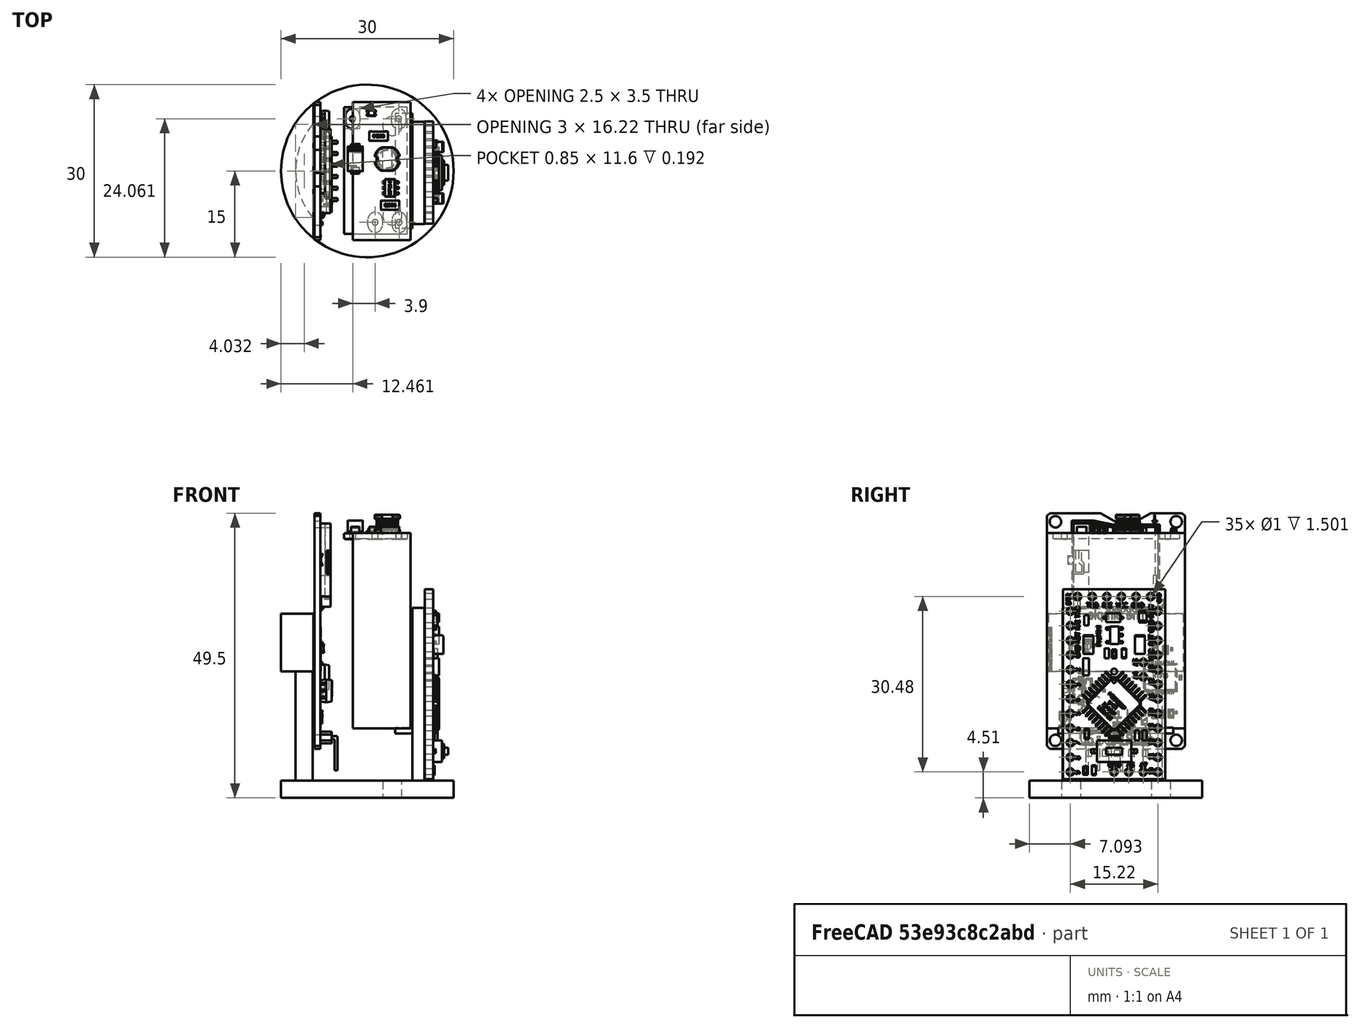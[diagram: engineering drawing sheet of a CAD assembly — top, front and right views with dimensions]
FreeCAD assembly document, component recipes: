
FREECAD ASSEMBLY — COMPONENT RECIPES ("case")

This assembly document has 2 components, labeled P0..P1 below (a component is one placed body or linked part). 2 of them carry a construction recipe — the FreeCAD feature program that regenerates the part from scratch, quoted from this document or its linked companion documents; the rest are supplied as boundary geometry only. No exploded tour is included for this assembly.
COMPONENT P0 — recipe-attached ("Case", modeled in this document).
Construction recipe (the document's own serialized feature program — sketch geometry with constraints, then the solid features built on it; lengths are millimeters unless a unit is written):

FEATURE [Sketcher::SketchObject] Sketch001
  ArcFitTolerance = 1e-06
  AttachmentSupport = -> [XY_Plane001]
  FullyConstrained = true
  MakeInternals = false
  MapMode = 5
  sketch-geometry (1):
    g0: Circle CenterX=0 CenterY=0 CenterZ=0 NormalX=0 NormalY=0 NormalZ=1 AngleXU=0 Radius=16.5
  constraints (2):
    c: Diameter(g0) = 33
    c: Coincident(g0,g-1)
FEATURE [PartDesign::Pad] Pad
  Direction = (0,0,1)
  Length = 1
  Length2 = 10
  Profile = -> Sketch001
  ReferenceAxis = -> Sketch001 [N_Axis]
  Refine = true
  Suppressed = false
  Type = 0
FEATURE [Sketcher::SketchObject] Sketch003
  ArcFitTolerance = 1e-06
  AttachmentSupport = -> [XY_Plane001]
  FullyConstrained = false
  MakeInternals = false
  MapMode = 5
  sketch-geometry (4):
    g0: LineSegment StartX=-10.1025 StartY=7.19243 StartZ=0 EndX=-10.8313 EndY=7.19243 EndZ=0
    g1: LineSegment StartX=-10.8313 StartY=7.19243 StartZ=0 EndX=-10.8313 EndY=-7.43647 EndZ=0
    g2: LineSegment StartX=-10.8313 StartY=-7.43647 StartZ=0 EndX=-10.1025 EndY=-7.43647 EndZ=0
    g3: LineSegment StartX=-10.1025 StartY=-7.43647 StartZ=0 EndX=-10.1025 EndY=7.19243 EndZ=0
  constraints (8):
    c: Coincident(g0,g1)
    c: Coincident(g1,g2)
    c: Coincident(g2,g3)
    c: Coincident(g3,g0)
    c: Horizontal(g0)
    c: Horizontal(g2)
    c: Vertical(g1)
    c: Vertical(g3)
FEATURE [Sketcher::SketchObject] Sketch004
  ArcFitTolerance = 1e-06
  AttachmentSupport = -> [Pad]
  FullyConstrained = false
  MakeInternals = false
  MapMode = 5
  Placement = pos=(0,0,1) rot=(0,0,1;0rad)
  sketch-geometry (4):
    g0: LineSegment StartX=-10.0742 StartY=4.3685 StartZ=0 EndX=-11.0742 EndY=4.3685 EndZ=0
    g1: LineSegment StartX=-11.0742 StartY=4.3685 StartZ=0 EndX=-11.0742 EndY=-5.47094 EndZ=0
    g2: LineSegment StartX=-11.0742 StartY=-5.47094 StartZ=0 EndX=-10.0742 EndY=-5.47094 EndZ=0
    g3: LineSegment StartX=-10.0742 StartY=-5.47094 StartZ=0 EndX=-10.0742 EndY=4.3685 EndZ=0
  constraints (9):
    c: Coincident(g0,g1)
    c: Coincident(g1,g2)
    c: Coincident(g2,g3)
    c: Coincident(g3,g0)
    c: Horizontal(g0)
    c: Horizontal(g2)
    c: Vertical(g1)
    c: Vertical(g3)
    c: Distance(g1,g3) = 1
FEATURE [PartDesign::Pocket] Pocket
  BaseFeature = -> Pad
  Direction = (0,0,-1)
  Length = 5
  Length2 = 5
  Profile = -> Sketch004
  ReferenceAxis = -> Sketch004 [N_Axis]
  Refine = true
  Suppressed = false
  Type = 0
FEATURE [Sketcher::SketchObject] Sketch005
  ArcFitTolerance = 1e-06
  AttachmentSupport = -> [Pocket]
  FullyConstrained = false
  MakeInternals = false
  MapMode = 5
  Placement = pos=(0,0,1) rot=(0,0,1;0rad)
  sketch-geometry (4):
    g0: LineSegment StartX=9.95573 StartY=8.56673 StartZ=0 EndX=7.83459 EndY=8.56673 EndZ=0
    g1: LineSegment StartX=7.83459 StartY=8.56673 StartZ=0 EndX=7.83459 EndY=-9.23192 EndZ=0
    g2: LineSegment StartX=7.83459 StartY=-9.23192 StartZ=0 EndX=9.95573 EndY=-9.23192 EndZ=0
    g3: LineSegment StartX=9.95573 StartY=-9.23192 StartZ=0 EndX=9.95573 EndY=8.56673 EndZ=0
  constraints (8):
    c: Coincident(g0,g1)
    c: Coincident(g1,g2)
    c: Coincident(g2,g3)
    c: Coincident(g3,g0)
    c: Horizontal(g0)
    c: Horizontal(g2)
    c: Vertical(g1)
    c: Vertical(g3)
FEATURE [PartDesign::Pad] Pad002
  BaseFeature = -> Pocket
  Direction = (0,0,1)
  Length = 30
  Length2 = 10
  Profile = -> Sketch005
  ReferenceAxis = -> Sketch005 [N_Axis]
  Refine = true
  Suppressed = false
  Type = 0
FEATURE [Sketcher::SketchObject] Sketch006
  ArcFitTolerance = 1e-06
  AttachmentSupport = -> [Pad002]
  FullyConstrained = false
  MakeInternals = false
  MapMode = 5
  Placement = pos=(0,0,0) rot=(1,0,0;3.14159rad)
  sketch-geometry (2):
    g0: LineSegment StartX=-9.46997 StartY=8.10814 StartZ=0 EndX=-9.46997 EndY=-8.10814 EndZ=0
    g1: ArcOfCircle CenterX=0 CenterY=0 CenterZ=0 NormalX=0 NormalY=0 NormalZ=1 AngleXU=0 Radius=12.4668 StartAngle=2.43351 EndAngle=3.84967
  constraints (3):
    c: Vertical(g0)
    c: Coincident(g1,g0)
    c: Coincident(g1,g0)
FEATURE [PartDesign::Pad] Pad003
  BaseFeature = -> Pad002
  Direction = (0,0,-1)
  Length = 30
  Length2 = 10
  Profile = -> Sketch006
  ReferenceAxis = -> Sketch006 [N_Axis]
  Refine = true
  Reversed = true
  Suppressed = false
  Type = 0
FEATURE [Sketcher::SketchObject] Sketch007
  ArcFitTolerance = 1e-06
  AttachmentSupport = -> [Pad003]
  FullyConstrained = false
  MakeInternals = false
  MapMode = 5
  Placement = pos=(7.83459,0,0) rot=(0.57735,-0.57735,-0.57735;2.0944rad)
  sketch-geometry (4):
    g0: LineSegment StartX=-10 StartY=6.21939 StartZ=0 EndX=-10 EndY=5.1638 EndZ=0
    g1: LineSegment StartX=-10 StartY=5.1638 StartZ=0 EndX=10 EndY=5.1638 EndZ=0
    g2: LineSegment StartX=10 StartY=5.1638 StartZ=0 EndX=10 EndY=6.21939 EndZ=0
    g3: LineSegment StartX=10 StartY=6.21939 StartZ=0 EndX=-10 EndY=6.21939 EndZ=0
  constraints (8):
    c: Coincident(g0,g1)
    c: Coincident(g1,g2)
    c: Coincident(g2,g3)
    c: Coincident(g3,g0)
    c: Vertical(g0)
    c: Vertical(g2)
    c: Horizontal(g1)
    c: Horizontal(g3)
FEATURE [PartDesign::Pad] Pad004
  BaseFeature = -> Pad003
  Direction = (-1,0,0)
  Length = 3
  Length2 = 10
  Profile = -> Sketch007
  ReferenceAxis = -> Sketch007 [N_Axis]
  Refine = true
  Suppressed = false
  Type = 0
FEATURE [Sketcher::SketchObject] Sketch
  ArcFitTolerance = 1e-06
  AttachmentSupport = -> [Pad004]
  FullyConstrained = false
  MakeInternals = false
  MapMode = 5
  Placement = pos=(0,0,30) rot=(0,0,1;0rad)
  sketch-geometry (2):
    g0: ArcOfCircle CenterX=0 CenterY=-0.00563305 CenterZ=0 NormalX=0 NormalY=0 NormalZ=1 AngleXU=0 Radius=16.4954 StartAngle=2.17527 EndAngle=4.10791
    g1: LineSegment StartX=-9.37485 StartY=13.5667 StartZ=0 EndX=-9.37485 EndY=-13.578 EndZ=0
  constraints (3):
    c: Coincident(g1,g0)
    c: Coincident(g1,g0)
    c: Vertical(g1)
FEATURE [PartDesign::Pad] Pad005
  BaseFeature = -> Pad004
  Direction = (0,0,1)
  Length = 10
  Length2 = 10
  Profile = -> Sketch
  ReferenceAxis = -> Sketch [N_Axis]
  Refine = true
  Reversed = true
  Suppressed = false
  Type = 0
FEATURE [Sketcher::SketchObject] Sketch008
  ArcFitTolerance = 1e-06
  AttachmentSupport = -> [Pad005]
  FullyConstrained = false
  MakeInternals = false
  MapMode = 5
  Placement = pos=(0,0,1) rot=(0,0,1;0rad)
  sketch-geometry (2):
    g0: Circle CenterX=4.36794 CenterY=-7.78214 CenterZ=0 NormalX=0 NormalY=0 NormalZ=1 AngleXU=0 Radius=1.55798
    g1: Circle CenterX=4.35381 CenterY=7.76956 CenterZ=0 NormalX=0 NormalY=0 NormalZ=1 AngleXU=0 Radius=1.55627
FEATURE [PartDesign::Pocket] Pocket001
  BaseFeature = -> Pad005
  Direction = (0,0,-1)
  Length = 5
  Length2 = 5
  Profile = -> Sketch008
  ReferenceAxis = -> Sketch008 [N_Axis]
  Refine = true
  Suppressed = false
  Type = 0
FEATURE [PartDesign::Pad] Pad006
  BaseFeature = -> Pocket001
  Direction = (0,0,-1)
  Length = 2
  Length2 = 10
  Profile = -> Pocket001 [Face2]
  Refine = true
  Suppressed = false
  Type = 0
FEATURE [Sketcher::SketchObject] Sketch009
  ArcFitTolerance = 1e-06
  AttachmentSupport = -> [Pad006]
  FullyConstrained = true
  MakeInternals = false
  MapMode = 5
  Placement = pos=(0,0,-2) rot=(1,0,0;3.14159rad)
  sketch-geometry (2):
    g0: Circle CenterX=0 CenterY=0 CenterZ=0 NormalX=0 NormalY=0 NormalZ=1 AngleXU=0 Radius=15.5
    g1: Circle CenterX=0 CenterY=0 CenterZ=0 NormalX=0 NormalY=0 NormalZ=1 AngleXU=0 Radius=16.5
  constraints (4):
    c: Diameter(g0) = 31
    c: Coincident(g0,g-1)
    c: Diameter(g1) = 33
    c: Coincident(g1,g0)
FEATURE [PartDesign::Pocket] Pocket002
  BaseFeature = -> Pad006
  Direction = (0,0,1)
  Length = 300
  Length2 = 5
  Profile = -> Sketch009
  ReferenceAxis = -> Sketch009 [N_Axis]
  Refine = true
  Suppressed = false
  Type = 0
FEATURE [PartDesign::Pad] Pad007
  BaseFeature = -> Pocket002
  Direction = (0,0,1)
  Length = 4
  Length2 = 10
  Profile = -> Pocket002 [Face21]
  Refine = true
  Suppressed = false
  Type = 0
FEATURE [PartDesign::Pocket] Pocket003
  BaseFeature = -> Pad007
  Direction = (0,0,1)
  Length = 4
  Length2 = 5
  Profile = -> Pad007 [Face15]
  Refine = true
  Suppressed = false
  Type = 0
FEATURE [Sketcher::SketchObject] Sketch010
  ArcFitTolerance = 1e-06
  AttachmentSupport = -> [Pocket003]
  FullyConstrained = true
  MakeInternals = false
  MapMode = 5
  Placement = pos=(0,0,-2) rot=(1,0,0;3.14159rad)
  sketch-geometry (2):
    g0: Circle CenterX=0 CenterY=0 CenterZ=0 NormalX=0 NormalY=0 NormalZ=1 AngleXU=0 Radius=15.5
    g1: Circle CenterX=0 CenterY=0 CenterZ=0 NormalX=0 NormalY=0 NormalZ=1 AngleXU=0 Radius=15
  constraints (4):
    c: Diameter(g0) = 31
    c: Coincident(g0,g-1)
    c: Diameter(g1) = 30
    c: Coincident(g1,g0)
FEATURE [PartDesign::Pocket] Pocket004
  BaseFeature = -> Pocket003
  Direction = (0,0,1)
  Length = 600
  Length2 = 5
  Profile = -> Sketch010
  ReferenceAxis = -> Sketch010 [N_Axis]
  Refine = true
  Suppressed = false
  Type = 0
FEATURE [Sketcher::SketchObject] Sketch011
  ArcFitTolerance = 1e-06
  AttachmentSupport = -> [Pocket004]
  FullyConstrained = false
  MakeInternals = false
  MapMode = 5
  Placement = pos=(0,0,-2) rot=(1,0,0;3.14159rad)
  sketch-geometry (4):
    g0: Circle CenterX=4.33918 CenterY=-7.8017 CenterZ=0 NormalX=0 NormalY=0 NormalZ=1 AngleXU=0 Radius=1.58527
    g1: Circle CenterX=4.33918 CenterY=-7.8017 CenterZ=0 NormalX=0 NormalY=0 NormalZ=1 AngleXU=0 Radius=1.65
    g2: Circle CenterX=4.36352 CenterY=7.76627 CenterZ=0 NormalX=0 NormalY=0 NormalZ=1 AngleXU=0 Radius=1.56339
    g3: Circle CenterX=4.36352 CenterY=7.76627 CenterZ=0 NormalX=0 NormalY=0 NormalZ=1 AngleXU=0 Radius=1.65
  constraints (4):
    c: Diameter(g1) = 3.3
    c: Coincident(g1,g0)
    c: Diameter(g3) = 3.3
    c: Coincident(g3,g2)
FEATURE [PartDesign::Pocket] Pocket005
  BaseFeature = -> Pocket004
  Direction = (0,0,1)
  Length = 8
  Length2 = 5
  Profile = -> Sketch011
  ReferenceAxis = -> Sketch011 [N_Axis]
  Refine = true
  Suppressed = false
  Type = 0
FEATURE [PartDesign::Body] Body  label="Case"
  AllowCompound = false
  Group = -> [Sketch001,Pad,Sketch003,Sketch004,Pocket,Sketch005,Pad002,Sketch006,Pad003,Sketch007,Pad004,Sketch,Pad005,Sketch008,Pocket001,Pad006,Sketch009,Pocket002,Pad007,Pocket003,Sketch010,Pocket004,Sketch011,Pocket005]
  Origin = -> Origin001
  Tip = -> Pocket005
COMPONENT P1 — recipe-attached ("lipo", modeled in this document).
Construction recipe (the document's own serialized feature program — sketch geometry with constraints, then the solid features built on it; lengths are millimeters unless a unit is written):

FEATURE [Sketcher::SketchObject] Sketch002
  ArcFitTolerance = 1e-06
  AttachmentSupport = -> [XY_Plane002]
  FullyConstrained = true
  MakeInternals = false
  MapMode = 5
  sketch-geometry (4):
    g0: LineSegment StartX=0 StartY=0 StartZ=0 EndX=0 EndY=-24 EndZ=0
    g1: LineSegment StartX=0 StartY=-24 StartZ=0 EndX=34 EndY=-24 EndZ=0
    g2: LineSegment StartX=34 StartY=-24 StartZ=0 EndX=34 EndY=0 EndZ=0
    g3: LineSegment StartX=34 StartY=0 StartZ=0 EndX=0 EndY=0 EndZ=0
  constraints (11):
    c: Coincident(g0,g1)
    c: Coincident(g1,g2)
    c: Coincident(g2,g3)
    c: Coincident(g3,g0)
    c: Vertical(g0)
    c: Vertical(g2)
    c: Horizontal(g1)
    c: Horizontal(g3)
    c: Distance(g0,g2) = 34
    c: Distance(g1,g3) = 24
    c: Coincident(g0,g-1)
FEATURE [PartDesign::Pad] Pad001
  Direction = (0,0,1)
  Length = 10
  Length2 = 10
  Profile = -> Sketch002
  ReferenceAxis = -> Sketch002 [N_Axis]
  Refine = true
  Suppressed = false
  Type = 0
FEATURE [PartDesign::Body] Body001  label="lipo"
  AllowCompound = false
  Group = -> [Sketch002,Pad001]
  Origin = -> Origin002
  Placement = pos=(7.5,12,10.07) rot=(0,1,0;4.71239rad)
  Tip = -> Pad001
PROVENANCE & LICENSES
A FreeCAD (.FCStd) document from a public repository crawl; recipes are the document's own serialized feature recipes (and, for linked parts, companion documents' recipes).
License: as declared in the source repository (recorded in the dataset sidecar).
